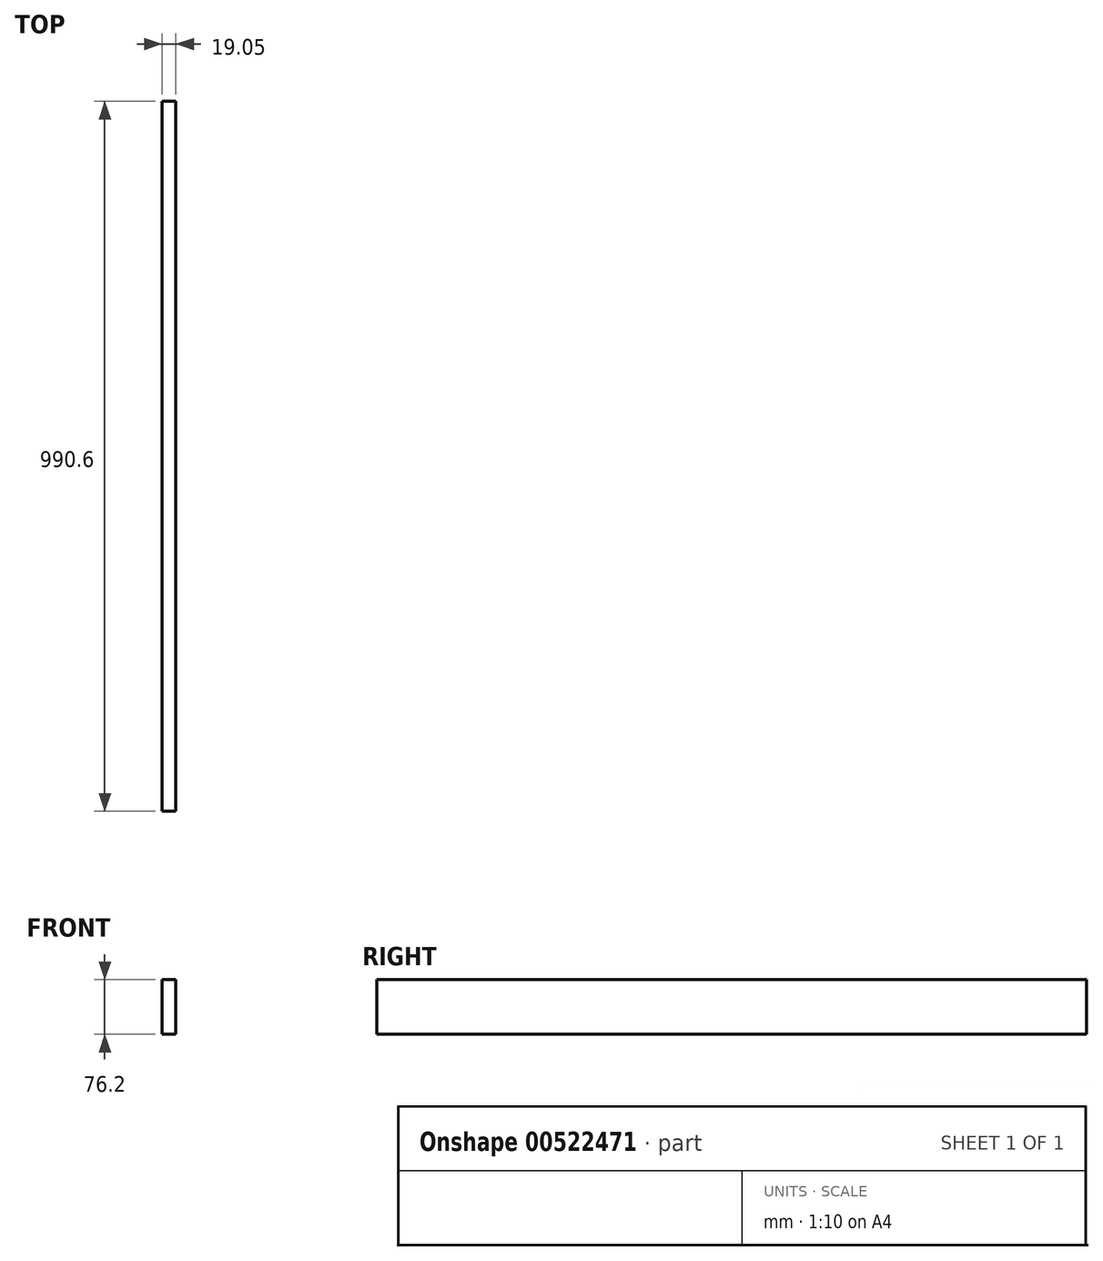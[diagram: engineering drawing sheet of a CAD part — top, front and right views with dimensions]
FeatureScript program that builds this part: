
annotation { "Feature Type Name" : "Feature", "Feature Type Description" : "" }
export const myFeature = defineFeature(function(context is Context, id is Id, definition is map)
    precondition{}
    {
        {
            var Q0;
            Q0=qCreatedBy(makeId("Top.planeOp"),FACE);
            var sketch = newSketch(context, id + "F0", { "sketchPlane" : qUnion([Q0])});
            skLineSegment(sketch, "E0.bottom", {"start": v(0, 587.79) * mm, "end": v(19.05, 587.79) * mm});
            skLineSegment(sketch, "E0.top", {"start": v(0, -402.81) * mm, "end": v(19.05, -402.81) * mm});
            skLineSegment(sketch, "E0.left", {"start": v(0, 587.79) * mm, "end": v(0, -402.81) * mm});
            skLineSegment(sketch, "E0.right", {"start": v(19.05, 587.79) * mm, "end": v(19.05, -402.81) * mm});
            skSolve(sketch);
        }
        {
            var Q0;
            Q0=makeQuery(id+"F0.imprint","IMPRINT",FACE,{"disambiguationData":[TD([[makeQuery(id+"F0.imprint","IMPRINT",EDGE,{"derivedFrom":sQuery(id+"F0.wireOp",EDGE,"E0.bottom")}),-1.0]])]});
            extrude(context, id + "F1", {"entities" : qUnion([Q0]), "depth" : 76.2 * mm, "offsetDistance" : 25.4 * mm});
        }
    });
